# Revit family: Faucet-Kitchen-KOHLER-KUMIN-K-99480T_1
name_source: partatom
category: Plumbing Fixtures
revit_build: Autodesk Revit 2017 (Build: 20160225_1515(x64)
units: mm (PartAtom-declared; Revit-internal decimal feet)

## family parameters
Cut with Voids When Loaded = No
Host = Face
OmniClass Number = 23.31.11.00
OmniClass Title = Faucets
Part Type = Normal
Room Calculation Point = No
Round Connector Dimension = Use Diameter
Shared = No

## types (4) — shared parameters
ADA Compliant = No
Assembly Code = D2010
CW Connection = Yes
Cold Water Inlet = Cold Water Inlet
Date Modified = 07/03/2020
Default Elevation = 36"
Drain Included = No
Finish = Kohler-Metal-CP-Polished_Chrome
Flow Rate = 2 GPM
HW Connection = Yes
Handle Clearance = 3 1/4"
Height = 13 1/2"
Hot Water Inlet = Hot Water Inlet
Length = 8 15/16"
Manufacturer = KOHLER Co.
Master Format 2014 = 22 41 39
Master Format 2014 Name = Residential Faucets, Supplies, and Trim
Material = Premium Metal Construction
Product Name = KUMIN
Spout Reach = 8 15/16"
URL = http://www.kohler.com.cn
Vent Connection = No
Waste Connection = No
Waste Water Outlet = Waste Water Outlet
WaterSense Certified = No
Width = 3 3/8"

## per-type parameters (varying)
| type | Description | Model | Pressure | Product Documentation Link | Product Page URL | Type |
| CP-Polished Chrome | Single-handle kitchen faucet | K-99480T-4-CP | 45.00 psi | http://files.kohler.com.cn | https://www.kohler.com.cn | 1 |
| 4E, CP-Polished Chrome | TUBE SPOUT KITCHEN FAUCET | K-99480T-4E-CP | 60.00 psi |  |  | 2 |
| 4E2, CP-Polished Chrome | TUBE SPOUT KITCHEN FAUCET | K-99480T-4E2-CP | 60.00 psi |  |  | 3 |
| 4CD, CP-Polished Chrome | COLD WATER KITCHEN FAUCET | K-99480T-4CD-CP | 60.00 psi |  |  | 4 |

## geometry (parser evidence)
native form markers: Sweep x5
no freeform markers — native parametric forms only
